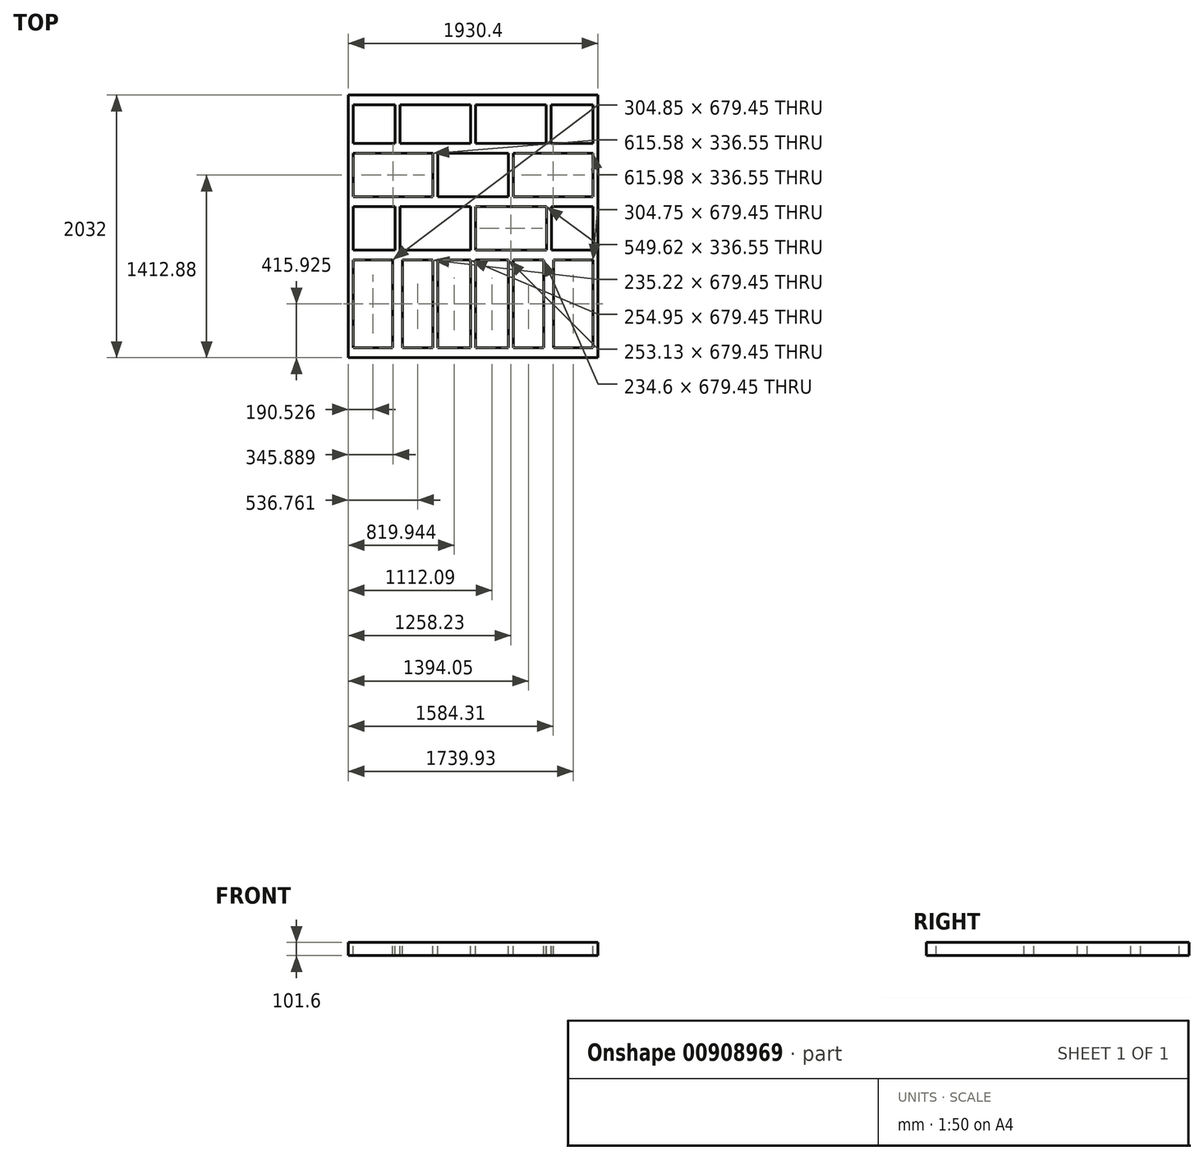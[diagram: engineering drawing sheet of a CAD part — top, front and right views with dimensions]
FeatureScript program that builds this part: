
annotation { "Feature Type Name" : "Feature", "Feature Type Description" : "" }
export const myFeature = defineFeature(function(context is Context, id is Id, definition is map)
    precondition{}
    {
        {
            var Q0;
            Q0=qCreatedBy(makeId("Top.planeOp"),FACE);
            var sketch = newSketch(context, id + "F0", { "sketchPlane" : qUnion([Q0])});
            skLineSegment(sketch, "E0.bottom", {"start": v(1892.3, 0) * mm, "end": v(1930.4, 0) * mm});
            skLineSegment(sketch, "E0.top", {"start": v(1892.3, 2032) * mm, "end": v(1930.4, 2032) * mm});
            skLineSegment(sketch, "E0.left", {"start": v(1892.3, 0) * mm, "end": v(1892.3, 2032) * mm});
            skLineSegment(sketch, "E0.right", {"start": v(1930.4, 0) * mm, "end": v(1930.4, 2032) * mm});
            skLineSegment(sketch, "E1.bottom", {"start": v(38.1, 2032) * mm, "end": v(1892.3, 2032) * mm});
            skLineSegment(sketch, "E1.top", {"start": v(38.1, 1993.9) * mm, "end": v(1892.3, 1993.9) * mm});
            skLineSegment(sketch, "E1.left", {"start": v(38.1, 2032) * mm, "end": v(38.1, 1993.9) * mm});
            skLineSegment(sketch, "E1.right", {"start": v(1892.3, 2032) * mm, "end": v(1892.3, 1993.9) * mm});
            skLineSegment(sketch, "E2.top", {"start": v(38.1, 1955.8) * mm, "end": v(1892.3, 1955.8) * mm});
            skLineSegment(sketch, "E2.left", {"start": v(38.1, 1993.9) * mm, "end": v(38.1, 1955.8) * mm});
            skLineSegment(sketch, "E2.right", {"start": v(1892.3, 1993.9) * mm, "end": v(1892.3, 1955.8) * mm});
            skLineSegment(sketch, "E3.bottom", {"start": v(38.1, 76.2) * mm, "end": v(1892.3, 76.2) * mm});
            skLineSegment(sketch, "E3.top", {"start": v(38.1, 38.1) * mm, "end": v(1892.3, 38.1) * mm});
            skLineSegment(sketch, "E3.left", {"start": v(38.1, 76.2) * mm, "end": v(38.1, 38.1) * mm});
            skLineSegment(sketch, "E3.right", {"start": v(1892.3, 76.2) * mm, "end": v(1892.3, 38.1) * mm});
            skLineSegment(sketch, "E4.top", {"start": v(38.1, 0) * mm, "end": v(1892.3, 0) * mm});
            skLineSegment(sketch, "E4.left", {"start": v(38.1, 38.1) * mm, "end": v(38.1, 0) * mm});
            skLineSegment(sketch, "E4.right", {"start": v(1892.3, 38.1) * mm, "end": v(1892.3, 0) * mm});
            skLineSegment(sketch, "E5.bottom", {"start": v(38.1, 1657.35) * mm, "end": v(1892.3, 1657.35) * mm});
            skLineSegment(sketch, "E5.top", {"start": v(38.1, 1619.25) * mm, "end": v(1892.3, 1619.25) * mm});
            skLineSegment(sketch, "E5.left", {"start": v(38.1, 1657.35) * mm, "end": v(38.1, 1619.25) * mm});
            skLineSegment(sketch, "E5.right", {"start": v(1892.3, 1657.35) * mm, "end": v(1892.3, 1619.25) * mm});
            skLineSegment(sketch, "E6.top", {"start": v(38.1, 1581.15) * mm, "end": v(1892.3, 1581.15) * mm});
            skLineSegment(sketch, "E6.left", {"start": v(38.1, 1619.25) * mm, "end": v(38.1, 1581.15) * mm});
            skLineSegment(sketch, "E6.right", {"start": v(1892.3, 1619.25) * mm, "end": v(1892.3, 1581.15) * mm});
            skLineSegment(sketch, "E7.bottom", {"start": v(38.1, 1244.6) * mm, "end": v(1892.3, 1244.6) * mm});
            skLineSegment(sketch, "E7.top", {"start": v(38.1, 1206.5) * mm, "end": v(1892.3, 1206.5) * mm});
            skLineSegment(sketch, "E7.left", {"start": v(38.1, 1244.6) * mm, "end": v(38.1, 1206.5) * mm});
            skLineSegment(sketch, "E7.right", {"start": v(1892.3, 1244.6) * mm, "end": v(1892.3, 1206.5) * mm});
            skLineSegment(sketch, "E8.top", {"start": v(38.1, 1168.4) * mm, "end": v(1892.3, 1168.4) * mm});
            skLineSegment(sketch, "E8.left", {"start": v(38.1, 1206.5) * mm, "end": v(38.1, 1168.4) * mm});
            skLineSegment(sketch, "E8.right", {"start": v(1892.3, 1206.5) * mm, "end": v(1892.3, 1168.4) * mm});
            skLineSegment(sketch, "E9.bottom", {"start": v(38.1, 831.85) * mm, "end": v(1892.3, 831.85) * mm});
            skLineSegment(sketch, "E9.top", {"start": v(38.1, 793.75) * mm, "end": v(1892.3, 793.75) * mm});
            skLineSegment(sketch, "E9.left", {"start": v(38.1, 831.85) * mm, "end": v(38.1, 793.75) * mm});
            skLineSegment(sketch, "E9.right", {"start": v(1892.3, 831.85) * mm, "end": v(1892.3, 793.75) * mm});
            skLineSegment(sketch, "E10.top", {"start": v(38.1, 755.65) * mm, "end": v(1892.3, 755.65) * mm});
            skLineSegment(sketch, "E10.left", {"start": v(38.1, 793.75) * mm, "end": v(38.1, 755.65) * mm});
            skLineSegment(sketch, "E10.right", {"start": v(1892.3, 793.75) * mm, "end": v(1892.3, 755.65) * mm});
            skLineSegment(sketch, "E11.bottom", {"start": v(399.36, 1168.4) * mm, "end": v(361.26, 1168.4) * mm});
            skLineSegment(sketch, "E11.top", {"start": v(399.36, 831.85) * mm, "end": v(361.26, 831.85) * mm});
            skLineSegment(sketch, "E11.left", {"start": v(399.36, 1168.4) * mm, "end": v(399.36, 831.85) * mm});
            skLineSegment(sketch, "E11.right", {"start": v(361.26, 1168.4) * mm, "end": v(361.26, 831.85) * mm});
            skLineSegment(sketch, "E12.bottom", {"start": v(983.42, 1168.4) * mm, "end": v(945.32, 1168.4) * mm});
            skLineSegment(sketch, "E12.top", {"start": v(983.42, 831.85) * mm, "end": v(945.32, 831.85) * mm});
            skLineSegment(sketch, "E12.left", {"start": v(983.42, 1168.4) * mm, "end": v(983.42, 831.85) * mm});
            skLineSegment(sketch, "E12.right", {"start": v(945.32, 1168.4) * mm, "end": v(945.32, 831.85) * mm});
            skLineSegment(sketch, "E13.bottom", {"start": v(1571.13, 1168.4) * mm, "end": v(1533.03, 1168.4) * mm});
            skLineSegment(sketch, "E13.top", {"start": v(1571.13, 831.85) * mm, "end": v(1533.03, 831.85) * mm});
            skLineSegment(sketch, "E13.left", {"start": v(1571.13, 1168.4) * mm, "end": v(1571.13, 831.85) * mm});
            skLineSegment(sketch, "E13.right", {"start": v(1533.03, 1168.4) * mm, "end": v(1533.03, 831.85) * mm});
            skLineSegment(sketch, "E14.bottom", {"start": v(691.78, 1581.15) * mm, "end": v(653.68, 1581.15) * mm});
            skLineSegment(sketch, "E14.top", {"start": v(691.78, 1244.6) * mm, "end": v(653.68, 1244.6) * mm});
            skLineSegment(sketch, "E14.left", {"start": v(691.78, 1581.15) * mm, "end": v(691.78, 1244.6) * mm});
            skLineSegment(sketch, "E14.right", {"start": v(653.68, 1581.15) * mm, "end": v(653.68, 1244.6) * mm});
            skLineSegment(sketch, "E15.bottom", {"start": v(1276.32, 1581.15) * mm, "end": v(1238.22, 1581.15) * mm});
            skLineSegment(sketch, "E15.top", {"start": v(1276.32, 1244.6) * mm, "end": v(1238.22, 1244.6) * mm});
            skLineSegment(sketch, "E15.left", {"start": v(1276.32, 1581.15) * mm, "end": v(1276.32, 1244.6) * mm});
            skLineSegment(sketch, "E15.right", {"start": v(1238.22, 1581.15) * mm, "end": v(1238.22, 1244.6) * mm});
            skLineSegment(sketch, "E16.bottom", {"start": v(983.1, 1955.8) * mm, "end": v(945, 1955.8) * mm});
            skLineSegment(sketch, "E16.top", {"start": v(983.1, 1657.35) * mm, "end": v(945, 1657.35) * mm});
            skLineSegment(sketch, "E16.left", {"start": v(983.1, 1955.8) * mm, "end": v(983.1, 1657.35) * mm});
            skLineSegment(sketch, "E16.right", {"start": v(945, 1955.8) * mm, "end": v(945, 1657.35) * mm});
            skLineSegment(sketch, "E17.bottom", {"start": v(400.7, 1955.8) * mm, "end": v(362.6, 1955.8) * mm});
            skLineSegment(sketch, "E17.top", {"start": v(400.7, 1657.35) * mm, "end": v(362.6, 1657.35) * mm});
            skLineSegment(sketch, "E17.left", {"start": v(400.7, 1955.8) * mm, "end": v(400.7, 1657.35) * mm});
            skLineSegment(sketch, "E17.right", {"start": v(362.6, 1955.8) * mm, "end": v(362.6, 1657.35) * mm});
            skLineSegment(sketch, "E18.bottom", {"start": v(1569.18, 1955.8) * mm, "end": v(1531.08, 1955.8) * mm});
            skLineSegment(sketch, "E18.top", {"start": v(1569.18, 1657.35) * mm, "end": v(1531.08, 1657.35) * mm});
            skLineSegment(sketch, "E18.left", {"start": v(1569.18, 1955.8) * mm, "end": v(1569.18, 1657.35) * mm});
            skLineSegment(sketch, "E18.right", {"start": v(1531.08, 1955.8) * mm, "end": v(1531.08, 1657.35) * mm});
            skLineSegment(sketch, "E19.bottom", {"start": v(0, 0) * mm, "end": v(38.1, 0) * mm});
            skLineSegment(sketch, "E19.top", {"start": v(0, 2032) * mm, "end": v(38.1, 2032) * mm});
            skLineSegment(sketch, "E19.left", {"start": v(0, 0) * mm, "end": v(0, 2032) * mm});
            skLineSegment(sketch, "E19.right", {"start": v(38.1, 0) * mm, "end": v(38.1, 2032) * mm});
            skLineSegment(sketch, "E20", {"start": v(38.1, 755.65) * mm, "end": v(38.1, 76.2) * mm, "construction": true});
            skLineSegment(sketch, "E21", {"start": v(38.1, 793.75) * mm, "end": v(38.1, 831.85) * mm, "construction": true});
            skLineSegment(sketch, "E22", {"start": v(38.1, 1168.4) * mm, "end": v(38.1, 1206.5) * mm, "construction": true});
            skLineSegment(sketch, "E23", {"start": v(38.1, 1206.5) * mm, "end": v(38.1, 1244.6) * mm, "construction": true});
            skLineSegment(sketch, "E24", {"start": v(38.1, 1581.15) * mm, "end": v(38.1, 1619.25) * mm, "construction": true});
            skLineSegment(sketch, "E25", {"start": v(38.1, 1619.25) * mm, "end": v(38.1, 1657.35) * mm, "construction": true});
            skLineSegment(sketch, "E26", {"start": v(38.1, 1993.9) * mm, "end": v(38.1, 2032) * mm, "construction": true});
            skLineSegment(sketch, "E27", {"start": v(38.1, 793.75) * mm, "end": v(38.1, 755.65) * mm, "construction": true});
            skLineSegment(sketch, "E28.bottom", {"start": v(381.05, 755.65) * mm, "end": v(419.15, 755.65) * mm});
            skLineSegment(sketch, "E28.top", {"start": v(381.05, 76.2) * mm, "end": v(419.15, 76.2) * mm});
            skLineSegment(sketch, "E28.left", {"start": v(381.05, 755.65) * mm, "end": v(381.05, 76.2) * mm});
            skLineSegment(sketch, "E28.right", {"start": v(419.15, 755.65) * mm, "end": v(419.15, 76.2) * mm});
            skLineSegment(sketch, "E29.bottom", {"start": v(342.95, 755.65) * mm, "end": v(381.05, 755.65) * mm});
            skLineSegment(sketch, "E29.top", {"start": v(342.95, 76.2) * mm, "end": v(381.05, 76.2) * mm});
            skLineSegment(sketch, "E29.left", {"start": v(342.95, 755.65) * mm, "end": v(342.95, 76.2) * mm});
            skLineSegment(sketch, "E30.bottom", {"start": v(654.37, 755.65) * mm, "end": v(692.47, 755.65) * mm});
            skLineSegment(sketch, "E30.top", {"start": v(654.37, 76.2) * mm, "end": v(692.47, 76.2) * mm});
            skLineSegment(sketch, "E30.left", {"start": v(654.37, 755.65) * mm, "end": v(654.37, 76.2) * mm});
            skLineSegment(sketch, "E30.right", {"start": v(692.47, 755.65) * mm, "end": v(692.47, 76.2) * mm});
            skLineSegment(sketch, "E31.bottom", {"start": v(947.42, 755.65) * mm, "end": v(985.52, 755.65) * mm});
            skLineSegment(sketch, "E31.top", {"start": v(947.42, 76.2) * mm, "end": v(985.52, 76.2) * mm});
            skLineSegment(sketch, "E31.left", {"start": v(947.42, 755.65) * mm, "end": v(947.42, 76.2) * mm});
            skLineSegment(sketch, "E31.right", {"start": v(985.52, 755.65) * mm, "end": v(985.52, 76.2) * mm});
            skLineSegment(sketch, "E32.bottom", {"start": v(1238.65, 755.65) * mm, "end": v(1276.75, 755.65) * mm});
            skLineSegment(sketch, "E32.top", {"start": v(1238.65, 76.2) * mm, "end": v(1276.75, 76.2) * mm});
            skLineSegment(sketch, "E32.left", {"start": v(1238.65, 755.65) * mm, "end": v(1238.65, 76.2) * mm});
            skLineSegment(sketch, "E32.right", {"start": v(1276.75, 755.65) * mm, "end": v(1276.75, 76.2) * mm});
            skLineSegment(sketch, "E33.bottom", {"start": v(1549.45, 755.65) * mm, "end": v(1587.55, 755.65) * mm});
            skLineSegment(sketch, "E33.top", {"start": v(1549.45, 76.2) * mm, "end": v(1587.55, 76.2) * mm});
            skLineSegment(sketch, "E33.left", {"start": v(1549.45, 755.65) * mm, "end": v(1549.45, 76.2) * mm});
            skLineSegment(sketch, "E33.right", {"start": v(1587.55, 755.65) * mm, "end": v(1587.55, 76.2) * mm});
            skLineSegment(sketch, "E34.bottom", {"start": v(1511.35, 755.65) * mm, "end": v(1549.45, 755.65) * mm});
            skLineSegment(sketch, "E34.top", {"start": v(1511.35, 76.2) * mm, "end": v(1549.45, 76.2) * mm});
            skLineSegment(sketch, "E34.left", {"start": v(1511.35, 755.65) * mm, "end": v(1511.35, 76.2) * mm});
            skLineSegment(sketch, "E35", {"start": v(38.1, 1168.4) * mm, "end": v(38.1, 831.85) * mm, "construction": true});
            skLineSegment(sketch, "E36", {"start": v(38.1, 1244.6) * mm, "end": v(38.1, 1581.15) * mm, "construction": true});
            skLineSegment(sketch, "E37", {"start": v(38.1, 1657.35) * mm, "end": v(38.1, 1955.8) * mm, "construction": true});
            skSolve(sketch);
        }
        {
            var Q0;
            {var subQ0=sQuery(id+"F0.wireOp",EDGE,"E1.bottom");Q0=makeQuery(id+"F0.imprint","IMPRINT",FACE,{"disambiguationData":[TD([[makeQuery(id+"F0.imprint","IMPRINT",EDGE,{"derivedFrom":subQ0}),-1.0]])]});}
            var Q1;
            {var subQ5=sQuery(id+"F0.wireOp",EDGE,"E1.top");Q1=makeQuery(id+"F0.imprint","IMPRINT",FACE,{"disambiguationData":[TD([[makeQuery(id+"F0.imprint","IMPRINT",EDGE,{"derivedFrom":subQ5}),-1.0]])]});}
            var Q2;
            Q2=makeQuery(id+"F0.imprint","IMPRINT",FACE,{"disambiguationData":[TD([[makeQuery(id+"F0.imprint","IMPRINT",EDGE,{"derivedFrom":sQuery(id+"F0.wireOp",EDGE,"E1.left")}),-1.0]])]});
            var Q3;
            {var subQ0=sQuery(id+"F0.wireOp",EDGE,"E17.left");Q3=makeQuery(id+"F0.imprint","IMPRINT",FACE,{"disambiguationData":[TD([[makeQuery(id+"F0.imprint","IMPRINT",EDGE,{"derivedFrom":subQ0}),-1.0]])]});}
            var Q4;
            {var subQ9=sQuery(id+"F0.wireOp",EDGE,"E5.top");Q4=makeQuery(id+"F0.imprint","IMPRINT",FACE,{"disambiguationData":[TD([[makeQuery(id+"F0.imprint","IMPRINT",EDGE,{"derivedFrom":subQ9}),1.0]])]});}
            var Q5;
            {var subQ0=sQuery(id+"F0.wireOp",EDGE,"E16.left");Q5=makeQuery(id+"F0.imprint","IMPRINT",FACE,{"disambiguationData":[TD([[makeQuery(id+"F0.imprint","IMPRINT",EDGE,{"derivedFrom":subQ0}),-1.0]])]});}
            var Q6;
            {var subQ0=sQuery(id+"F0.wireOp",EDGE,"E18.left");Q6=makeQuery(id+"F0.imprint","IMPRINT",FACE,{"disambiguationData":[TD([[makeQuery(id+"F0.imprint","IMPRINT",EDGE,{"derivedFrom":subQ0}),-1.0]])]});}
            var Q7;
            {var subQ12=sQuery(id+"F0.wireOp",EDGE,"E0.bottom");Q7=makeQuery(id+"F0.imprint","IMPRINT",FACE,{"disambiguationData":[TD([[makeQuery(id+"F0.imprint","IMPRINT",EDGE,{"derivedFrom":subQ12}),1.0]])]});}
            var Q8;
            {var subQ0=sQuery(id+"F0.wireOp",EDGE,"E15.left");Q8=makeQuery(id+"F0.imprint","IMPRINT",FACE,{"disambiguationData":[TD([[makeQuery(id+"F0.imprint","IMPRINT",EDGE,{"derivedFrom":subQ0}),-1.0]])]});}
            var Q9;
            {var subQ0=sQuery(id+"F0.wireOp",EDGE,"E14.left");Q9=makeQuery(id+"F0.imprint","IMPRINT",FACE,{"disambiguationData":[TD([[makeQuery(id+"F0.imprint","IMPRINT",EDGE,{"derivedFrom":subQ0}),-1.0]])]});}
            var Q10;
            {var subQ8=sQuery(id+"F0.wireOp",EDGE,"E7.top");Q10=makeQuery(id+"F0.imprint","IMPRINT",FACE,{"disambiguationData":[TD([[makeQuery(id+"F0.imprint","IMPRINT",EDGE,{"derivedFrom":subQ8}),1.0]])]});}
            var Q11;
            {var subQ3=sQuery(id+"F0.wireOp",EDGE,"E7.top");Q11=makeQuery(id+"F0.imprint","IMPRINT",FACE,{"disambiguationData":[TD([[makeQuery(id+"F0.imprint","IMPRINT",EDGE,{"derivedFrom":subQ3}),-1.0]])]});}
            var Q12;
            {var subQ0=sQuery(id+"F0.wireOp",EDGE,"E11.left");Q12=makeQuery(id+"F0.imprint","IMPRINT",FACE,{"disambiguationData":[TD([[makeQuery(id+"F0.imprint","IMPRINT",EDGE,{"derivedFrom":subQ0}),-1.0]])]});}
            var Q13;
            {var subQ0=sQuery(id+"F0.wireOp",EDGE,"E12.left");Q13=makeQuery(id+"F0.imprint","IMPRINT",FACE,{"disambiguationData":[TD([[makeQuery(id+"F0.imprint","IMPRINT",EDGE,{"derivedFrom":subQ0}),-1.0]])]});}
            var Q14;
            {var subQ0=sQuery(id+"F0.wireOp",EDGE,"E13.left");Q14=makeQuery(id+"F0.imprint","IMPRINT",FACE,{"disambiguationData":[TD([[makeQuery(id+"F0.imprint","IMPRINT",EDGE,{"derivedFrom":subQ0}),-1.0]])]});}
            var Q15;
            {var subQ11=sQuery(id+"F0.wireOp",EDGE,"E9.top");Q15=makeQuery(id+"F0.imprint","IMPRINT",FACE,{"disambiguationData":[TD([[makeQuery(id+"F0.imprint","IMPRINT",EDGE,{"derivedFrom":subQ11}),-1.0]])]});}
            var Q16;
            {var subQ0=sQuery(id+"F0.wireOp",EDGE,"E33.left");Q16=makeQuery(id+"F0.imprint","IMPRINT",FACE,{"disambiguationData":[TD([[makeQuery(id+"F0.imprint","IMPRINT",EDGE,{"derivedFrom":subQ0}),1.0]])]});}
            var Q17;
            {var subQ0=sQuery(id+"F0.wireOp",EDGE,"E33.left");Q17=makeQuery(id+"F0.imprint","IMPRINT",FACE,{"disambiguationData":[TD([[makeQuery(id+"F0.imprint","IMPRINT",EDGE,{"derivedFrom":subQ0}),-1.0]])]});}
            var Q18;
            {var subQ2=sQuery(id+"F0.wireOp",EDGE,"E32.left");Q18=makeQuery(id+"F0.imprint","IMPRINT",FACE,{"disambiguationData":[TD([[makeQuery(id+"F0.imprint","IMPRINT",EDGE,{"derivedFrom":subQ2}),1.0]])]});}
            var Q19;
            {var subQ0=sQuery(id+"F0.wireOp",EDGE,"E31.left");Q19=makeQuery(id+"F0.imprint","IMPRINT",FACE,{"disambiguationData":[TD([[makeQuery(id+"F0.imprint","IMPRINT",EDGE,{"derivedFrom":subQ0}),1.0]])]});}
            var Q20;
            {var subQ0=sQuery(id+"F0.wireOp",EDGE,"E30.left");Q20=makeQuery(id+"F0.imprint","IMPRINT",FACE,{"disambiguationData":[TD([[makeQuery(id+"F0.imprint","IMPRINT",EDGE,{"derivedFrom":subQ0}),1.0]])]});}
            var Q21;
            {var subQ0=sQuery(id+"F0.wireOp",EDGE,"E28.left");Q21=makeQuery(id+"F0.imprint","IMPRINT",FACE,{"disambiguationData":[TD([[makeQuery(id+"F0.imprint","IMPRINT",EDGE,{"derivedFrom":subQ0}),1.0]])]});}
            var Q22;
            {var subQ0=sQuery(id+"F0.wireOp",EDGE,"E28.left");Q22=makeQuery(id+"F0.imprint","IMPRINT",FACE,{"disambiguationData":[TD([[makeQuery(id+"F0.imprint","IMPRINT",EDGE,{"derivedFrom":subQ0}),-1.0]])]});}
            var Q23;
            {var subQ10=sQuery(id+"F0.wireOp",EDGE,"E3.top");Q23=makeQuery(id+"F0.imprint","IMPRINT",FACE,{"disambiguationData":[TD([[makeQuery(id+"F0.imprint","IMPRINT",EDGE,{"derivedFrom":subQ10}),1.0]])]});}
            var Q24;
            {var subQ2=sQuery(id+"F0.wireOp",EDGE,"E3.top");Q24=makeQuery(id+"F0.imprint","IMPRINT",FACE,{"disambiguationData":[TD([[makeQuery(id+"F0.imprint","IMPRINT",EDGE,{"derivedFrom":subQ2}),-1.0]])]});}
            var Q25;
            {var subQ7=sQuery(id+"F0.wireOp",EDGE,"E9.top");Q25=makeQuery(id+"F0.imprint","IMPRINT",FACE,{"disambiguationData":[TD([[makeQuery(id+"F0.imprint","IMPRINT",EDGE,{"derivedFrom":subQ7}),1.0]])]});}
            var Q26;
            {var subQ3=sQuery(id+"F0.wireOp",EDGE,"E5.top");Q26=makeQuery(id+"F0.imprint","IMPRINT",FACE,{"disambiguationData":[TD([[makeQuery(id+"F0.imprint","IMPRINT",EDGE,{"derivedFrom":subQ3}),-1.0]])]});}
            var Q27;
            Q27=sQuery(id+"F0.wireOp",EDGE,"E3.top");
            var Q28;
            Q28=sQuery(id+"F0.wireOp",EDGE,"f4a54590-f679-470d-b17d-d7b63abae7a4.right");
            var Q29;
            Q29=sQuery(id+"F0.wireOp",EDGE,"E8.top");
            var Q30;
            Q30=sQuery(id+"F0.wireOp",EDGE,"E13.right");
            var Q31;
            Q31=sQuery(id+"F0.wireOp",EDGE,"E5.bottom");
            var Q32;
            Q32=sQuery(id+"F0.wireOp",EDGE,"f4a54590-f679-470d-b17d-d7b63abae7a4.left");
            var Q33;
            Q33=sQuery(id+"F0.wireOp",EDGE,"53bdea83-3857-4755-855b-8170dfc908b8.left");
            var Q34;
            Q34=sQuery(id+"F0.wireOp",EDGE,"E9.bottom");
            var Q35;
            Q35=sQuery(id+"F0.wireOp",EDGE,"9dd1a028-6e6e-4eb5-9ef6-384a2f4d258a.right");
            var Q36;
            Q36=sQuery(id+"F0.wireOp",EDGE,"E1.bottom");
            var Q37;
            Q37=sQuery(id+"F0.wireOp",EDGE,"E7.top");
            var Q38;
            Q38=sQuery(id+"F0.wireOp",EDGE,"E17.left");
            var Q39;
            Q39=sQuery(id+"F0.wireOp",EDGE,"7gxD3gMZ-yqXD-hXsp-ptNt-cMuwxghBR4hQ.left");
            var Q40;
            Q40=sQuery(id+"F0.wireOp",EDGE,"E16.left");
            var Q41;
            Q41=sQuery(id+"F0.wireOp",EDGE,"E7.bottom");
            var Q42;
            Q42=sQuery(id+"F0.wireOp",EDGE,"E18.right");
            var Q43;
            Q43=sQuery(id+"F0.wireOp",EDGE,"Xk9ZSXhl-9WVN-LsCH-6vrX-DO0PrP3blS64.right");
            var Q44;
            Q44=sQuery(id+"F0.wireOp",EDGE,"E10.top");
            var Q45;
            Q45=sQuery(id+"F0.wireOp",EDGE,"E9.top");
            var Q46;
            Q46=sQuery(id+"F0.wireOp",EDGE,"E15.left");
            var Q47;
            Q47=sQuery(id+"F0.wireOp",EDGE,"E14.right");
            var Q48;
            Q48=sQuery(id+"F0.wireOp",EDGE,"E15.right");
            var Q49;
            Q49=sQuery(id+"F0.wireOp",EDGE,"E4.top");
            var Q50;
            Q50=sQuery(id+"F0.wireOp",EDGE,"ec6ddc45-9126-4f8c-88d3-4725c3311ca4.left");
            var Q51;
            Q51=sQuery(id+"F0.wireOp",EDGE,"E6.top");
            var Q52;
            Q52=sQuery(id+"F0.wireOp",EDGE,"E14.left");
            var Q53;
            Q53=sQuery(id+"F0.wireOp",EDGE,"324f7306-f933-450f-91b4-e36e5f04ff58.left");
            var Q54;
            Q54=sQuery(id+"F0.wireOp",EDGE,"E17.right");
            var Q55;
            Q55=sQuery(id+"F0.wireOp",EDGE,"E1.top");
            var Q56;
            Q56=sQuery(id+"F0.wireOp",EDGE,"E2.top");
            var Q57;
            Q57=sQuery(id+"F0.wireOp",EDGE,"E11.left");
            var Q58;
            Q58=sQuery(id+"F0.wireOp",EDGE,"E0.left");
            var Q59;
            Q59=sQuery(id+"F0.wireOp",EDGE,"E5.top");
            var Q60;
            Q60=sQuery(id+"F0.wireOp",EDGE,"7gxD3gMZ-yqXD-hXsp-ptNt-cMuwxghBR4hQ.right");
            var Q61;
            Q61=sQuery(id+"F0.wireOp",EDGE,"E13.left");
            var Q62;
            Q62=sQuery(id+"F0.wireOp",EDGE,"E0.right");
            var Q63;
            Q63=sQuery(id+"F0.wireOp",EDGE,"53bdea83-3857-4755-855b-8170dfc908b8.right");
            var Q64;
            Q64=sQuery(id+"F0.wireOp",EDGE,"E12.right");
            var Q65;
            Q65=sQuery(id+"F0.wireOp",EDGE,"E12.left");
            var Q66;
            Q66=sQuery(id+"F0.wireOp",EDGE,"Xk9ZSXhl-9WVN-LsCH-6vrX-DO0PrP3blS64.left");
            var Q67;
            Q67=sQuery(id+"F0.wireOp",EDGE,"E11.right");
            var Q68;
            Q68=sQuery(id+"F0.wireOp",EDGE,"E18.left");
            var Q69;
            Q69=sQuery(id+"F0.wireOp",EDGE,"E16.right");
            var Q70;
            Q70=sQuery(id+"F0.wireOp",EDGE,"41d16305-1d51-44de-ace3-76fd3ee58c13.left");
            var Q71;
            Q71=sQuery(id+"F0.wireOp",EDGE,"9dd1a028-6e6e-4eb5-9ef6-384a2f4d258a.left");
            var Q72;
            Q72=sQuery(id+"F0.wireOp",EDGE,"E3.bottom");
            var Q73;
            Q73=sQuery(id+"F0.wireOp",EDGE,"81da6e28-c8a7-4bec-ad97-56e941f3560d.right");
            var Q74;
            Q74=sQuery(id+"F0.wireOp",EDGE,"E5.top");
            var Q75;
            Q75=sQuery(id+"F0.wireOp",EDGE,"324f7306-f933-450f-91b4-e36e5f04ff58.right");
            var Q76;
            Q76=sQuery(id+"F0.wireOp",EDGE,"E3.top");
            var Q77;
            Q77=sQuery(id+"F0.wireOp",EDGE,"e1a44880-0ee3-4b06-b7a8-56feda26d699.left");
            var Q78;
            Q78=sQuery(id+"F0.wireOp",EDGE,"ec6ddc45-9126-4f8c-88d3-4725c3311ca4.right");
            var Q79;
            Q79=sQuery(id+"F0.wireOp",EDGE,"E1.top");
            var Q80;
            Q80=sQuery(id+"F0.wireOp",EDGE,"E7.top");
            var Q81;
            Q81=sQuery(id+"F0.wireOp",EDGE,"E9.top");
            var Q82;
            Q82=sQuery(id+"F0.wireOp",EDGE,"63a9893d-4d6b-4cbd-98dc-a4ef5a0606dd.left");
            var Q83;
            Q83=sQuery(id+"F0.wireOp",EDGE,"81da6e28-c8a7-4bec-ad97-56e941f3560d.left");
            var Q84;
            Q84=sQuery(id+"F0.wireOp",EDGE,"E14.bottom");
            var Q85;
            Q85=sQuery(id+"F0.wireOp",EDGE,"E15.bottom");
            var Q86;
            Q86=sQuery(id+"F0.wireOp",EDGE,"E12.bottom");
            var Q87;
            Q87=sQuery(id+"F0.wireOp",EDGE,"E12.top");
            var Q88;
            Q88=sQuery(id+"F0.wireOp",EDGE,"53bdea83-3857-4755-855b-8170dfc908b8.top");
            var Q89;
            Q89=sQuery(id+"F0.wireOp",EDGE,"E18.top");
            var Q90;
            Q90=sQuery(id+"F0.wireOp",EDGE,"53bdea83-3857-4755-855b-8170dfc908b8.bottom");
            var Q91;
            Q91=sQuery(id+"F0.wireOp",EDGE,"E17.bottom");
            var Q92;
            Q92=sQuery(id+"F0.wireOp",EDGE,"E15.top");
            var Q93;
            Q93=sQuery(id+"F0.wireOp",EDGE,"E5.right");
            var Q94;
            Q94=sQuery(id+"F0.wireOp",EDGE,"E14.top");
            var Q95;
            Q95=sQuery(id+"F0.wireOp",EDGE,"E16.bottom");
            var Q96;
            Q96=sQuery(id+"F0.wireOp",EDGE,"E13.bottom");
            var Q97;
            Q97=sQuery(id+"F0.wireOp",EDGE,"E13.top");
            var Q98;
            Q98=sQuery(id+"F0.wireOp",EDGE,"E11.bottom");
            var Q99;
            Q99=sQuery(id+"F0.wireOp",EDGE,"E5.left");
            var Q100;
            Q100=sQuery(id+"F0.wireOp",EDGE,"E11.top");
            var Q101;
            Q101=sQuery(id+"F0.wireOp",EDGE,"E17.top");
            var Q102;
            Q102=sQuery(id+"F0.wireOp",EDGE,"E18.bottom");
            var Q103;
            Q103=sQuery(id+"F0.wireOp",EDGE,"E16.top");
            var Q104;
            Q104=sQuery(id+"F0.wireOp",EDGE,"9dd1a028-6e6e-4eb5-9ef6-384a2f4d258a.top");
            var Q105;
            Q105=sQuery(id+"F0.wireOp",EDGE,"324f7306-f933-450f-91b4-e36e5f04ff58.top");
            var Q106;
            Q106=sQuery(id+"F0.wireOp",EDGE,"324f7306-f933-450f-91b4-e36e5f04ff58.bottom");
            var Q107;
            Q107=sQuery(id+"F0.wireOp",EDGE,"9dd1a028-6e6e-4eb5-9ef6-384a2f4d258a.bottom");
            var Q108;
            Q108=sQuery(id+"F0.wireOp",EDGE,"E7.right");
            var Q109;
            Q109=sQuery(id+"F0.wireOp",EDGE,"81da6e28-c8a7-4bec-ad97-56e941f3560d.bottom");
            var Q110;
            Q110=sQuery(id+"F0.wireOp",EDGE,"E9.right");
            var Q111;
            Q111=sQuery(id+"F0.wireOp",EDGE,"E1.left");
            var Q112;
            Q112=sQuery(id+"F0.wireOp",EDGE,"E6.left");
            var Q113;
            Q113=sQuery(id+"F0.wireOp",EDGE,"E6.right");
            var Q114;
            Q114=sQuery(id+"F0.wireOp",EDGE,"E7.left");
            var Q115;
            Q115=sQuery(id+"F0.wireOp",EDGE,"Xk9ZSXhl-9WVN-LsCH-6vrX-DO0PrP3blS64.top");
            var Q116;
            Q116=sQuery(id+"F0.wireOp",EDGE,"E1.right");
            var Q117;
            Q117=sQuery(id+"F0.wireOp",EDGE,"E8.left");
            var Q118;
            Q118=sQuery(id+"F0.wireOp",EDGE,"E0.bottom");
            var Q119;
            Q119=sQuery(id+"F0.wireOp",EDGE,"Xk9ZSXhl-9WVN-LsCH-6vrX-DO0PrP3blS64.bottom");
            var Q120;
            Q120=sQuery(id+"F0.wireOp",EDGE,"7gxD3gMZ-yqXD-hXsp-ptNt-cMuwxghBR4hQ.top");
            var Q121;
            Q121=sQuery(id+"F0.wireOp",EDGE,"7gxD3gMZ-yqXD-hXsp-ptNt-cMuwxghBR4hQ.bottom");
            var Q122;
            Q122=sQuery(id+"F0.wireOp",EDGE,"E2.right");
            var Q123;
            Q123=sQuery(id+"F0.wireOp",EDGE,"81da6e28-c8a7-4bec-ad97-56e941f3560d.top");
            var Q124;
            Q124=sQuery(id+"F0.wireOp",EDGE,"E9.left");
            var Q125;
            Q125=sQuery(id+"F0.wireOp",EDGE,"E2.left");
            var Q126;
            Q126=sQuery(id+"F0.wireOp",EDGE,"E10.right");
            var Q127;
            Q127=sQuery(id+"F0.wireOp",EDGE,"E10.left");
            var Q128;
            Q128=sQuery(id+"F0.wireOp",EDGE,"ec6ddc45-9126-4f8c-88d3-4725c3311ca4.bottom");
            var Q129;
            Q129=sQuery(id+"F0.wireOp",EDGE,"f4a54590-f679-470d-b17d-d7b63abae7a4.bottom");
            var Q130;
            Q130=sQuery(id+"F0.wireOp",EDGE,"f4a54590-f679-470d-b17d-d7b63abae7a4.top");
            var Q131;
            Q131=sQuery(id+"F0.wireOp",EDGE,"ec6ddc45-9126-4f8c-88d3-4725c3311ca4.top");
            var Q132;
            Q132=sQuery(id+"F0.wireOp",EDGE,"E8.right");
            var Q133;
            Q133=sQuery(id+"F0.wireOp",EDGE,"E4.right");
            var Q134;
            Q134=sQuery(id+"F0.wireOp",EDGE,"E0.top");
            var Q135;
            Q135=sQuery(id+"F0.wireOp",EDGE,"E3.right");
            var Q136;
            Q136=sQuery(id+"F0.wireOp",EDGE,"E3.left");
            var Q137;
            Q137=sQuery(id+"F0.wireOp",EDGE,"E4.left");
            extrude(context, id + "F1", {"entities" : qUnion([Q0, Q1, Q2, Q3, Q4, Q5, Q6, Q7, Q8, Q9, Q10, Q11, Q12, Q13, Q14, Q15, Q16, Q17, Q18, Q19, Q20, Q21, Q22, Q23, Q24, Q25, Q26]), "surfaceEntities" : qUnion([Q27, Q28, Q29, Q30, Q31, Q32, Q33, Q34, Q35, Q36, Q37, Q38, Q39, Q40, Q41, Q42, Q43, Q44, Q45, Q46, Q47, Q48, Q49, Q50, Q51, Q52, Q53, Q54, Q55, Q56, Q57, Q58, Q59, Q60, Q61, Q62, Q63, Q64, Q65, Q66, Q67, Q68, Q69, Q70, Q71, Q72, Q73, Q74, Q75, Q76, Q77, Q78, Q79, Q80, Q81, Q82, Q83, Q84, Q85, Q86, Q87, Q88, Q89, Q90, Q91, Q92, Q93, Q94, Q95, Q96, Q97, Q98, Q99, Q100, Q101, Q102, Q103, Q104, Q105, Q106, Q107, Q108, Q109, Q110, Q111, Q112, Q113, Q114, Q115, Q116, Q117, Q118, Q119, Q120, Q121, Q122, Q123, Q124, Q125, Q126, Q127, Q128, Q129, Q130, Q131, Q132, Q133, Q134, Q135, Q136, Q137]), "depth" : -101.6 * mm, "offsetDistance" : 25.4 * mm});
        }
    });
